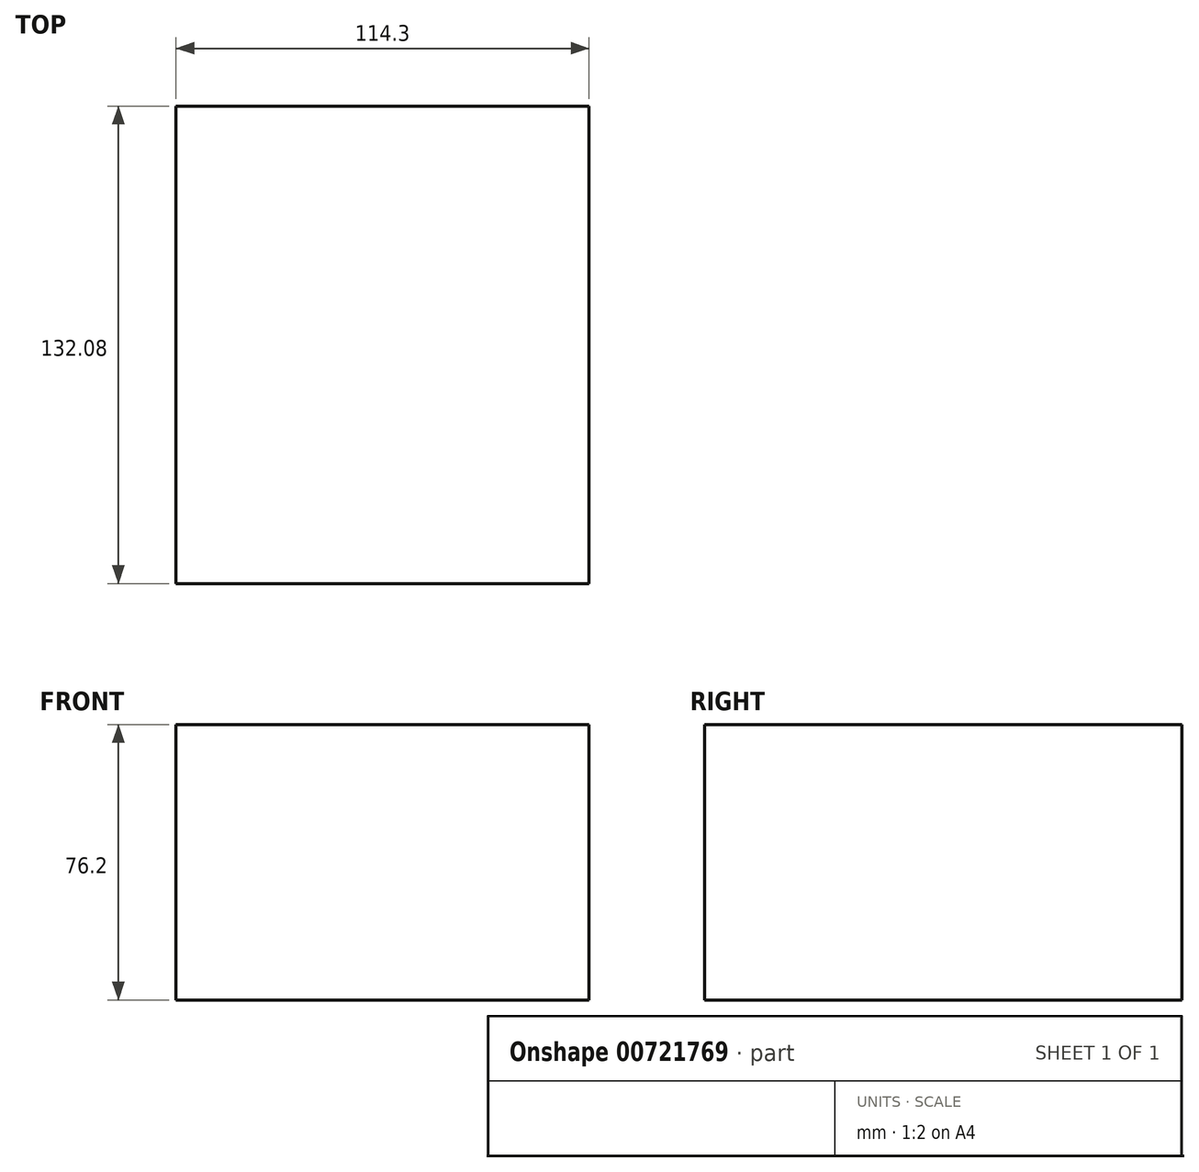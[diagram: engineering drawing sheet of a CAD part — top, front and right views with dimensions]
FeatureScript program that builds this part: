
annotation { "Feature Type Name" : "Feature", "Feature Type Description" : "" }
export const myFeature = defineFeature(function(context is Context, id is Id, definition is map)
    precondition{}
    {
        {
            var Q0;
            Q0=qCreatedBy(makeId("Front.planeOp"),FACE);
            var sketch = newSketch(context, id + "F0", { "sketchPlane" : qUnion([Q0])});
            skLineSegment(sketch, "E0.bottom", {"start": v(0, 0) * mm, "end": v(114.3, 0) * mm});
            skLineSegment(sketch, "E0.top", {"start": v(0, 76.2) * mm, "end": v(114.3, 76.2) * mm});
            skLineSegment(sketch, "E0.left", {"start": v(0, 0) * mm, "end": v(0, 76.2) * mm});
            skLineSegment(sketch, "E0.right", {"start": v(114.3, 0) * mm, "end": v(114.3, 76.2) * mm});
            skSolve(sketch);
        }
        {
            var Q0;
            Q0 = qSketchRegion(id + "F0", true);
            extrude(context, id + "F1", {"entities" : qUnion([Q0]), "endBound" : BoundingType.SYMMETRIC, "depth" : 132.08 * mm, "offsetDistance" : 25.4 * mm});
        }
        {
            var Q0;
            Q0=makeQuery(id+"F1.opExtrude","SWEPT_FACE",FACE,{"disambiguationData":[OSD([sQuery(id+"F0.wireOp",EDGE,"E0.top")])]});
            var Q1;
            Q1=makeQuery(id+"F1.opExtrude","CAP_EDGE",EDGE,{"disambiguationData":[OSD([sQuery(id+"F0.wireOp",EDGE,"E0.top")])],"isStart":false});
            cPlane(context, id + "F2", {"entities" : qUnion([Q0, Q1]), "cplaneType" : CPlaneType.LINE_ANGLE, "offset" : 35.56 * mm, "angle" : 45 * degree, "width" : 152.4 * mm, "height" : 152.4 * mm});
        }
        {
            var Q0;
            Q0=qCreatedBy(id+"F2.planeOp",FACE);
            var sketch = newSketch(context, id + "F3", { "sketchPlane" : qUnion([Q0])});
            skCircle(sketch, "E1", {"center": v(53.94, -7.67) * mm, "radius": 27.35 * mm});
            skSolve(sketch);
        }
        {
            var Q0;
            Q0=makeQuery(id+"F3.imprint","IMPRINT",FACE,{"disambiguationData":[TD([[makeQuery(id+"F3.imprint","IMPRINT",EDGE,{"derivedFrom":sQuery(id+"F3.wireOp",EDGE,"E1")}),1.0]])]});
            extrude(context, id + "F4", {"entities" : qUnion([Q0]), "operationType" : NewBodyOperationType.REMOVE, "endBound" : BoundingType.THROUGH_ALL, "depth" : 35.56 * mm, "offsetDistance" : 25.4 * mm});
        }
    });
